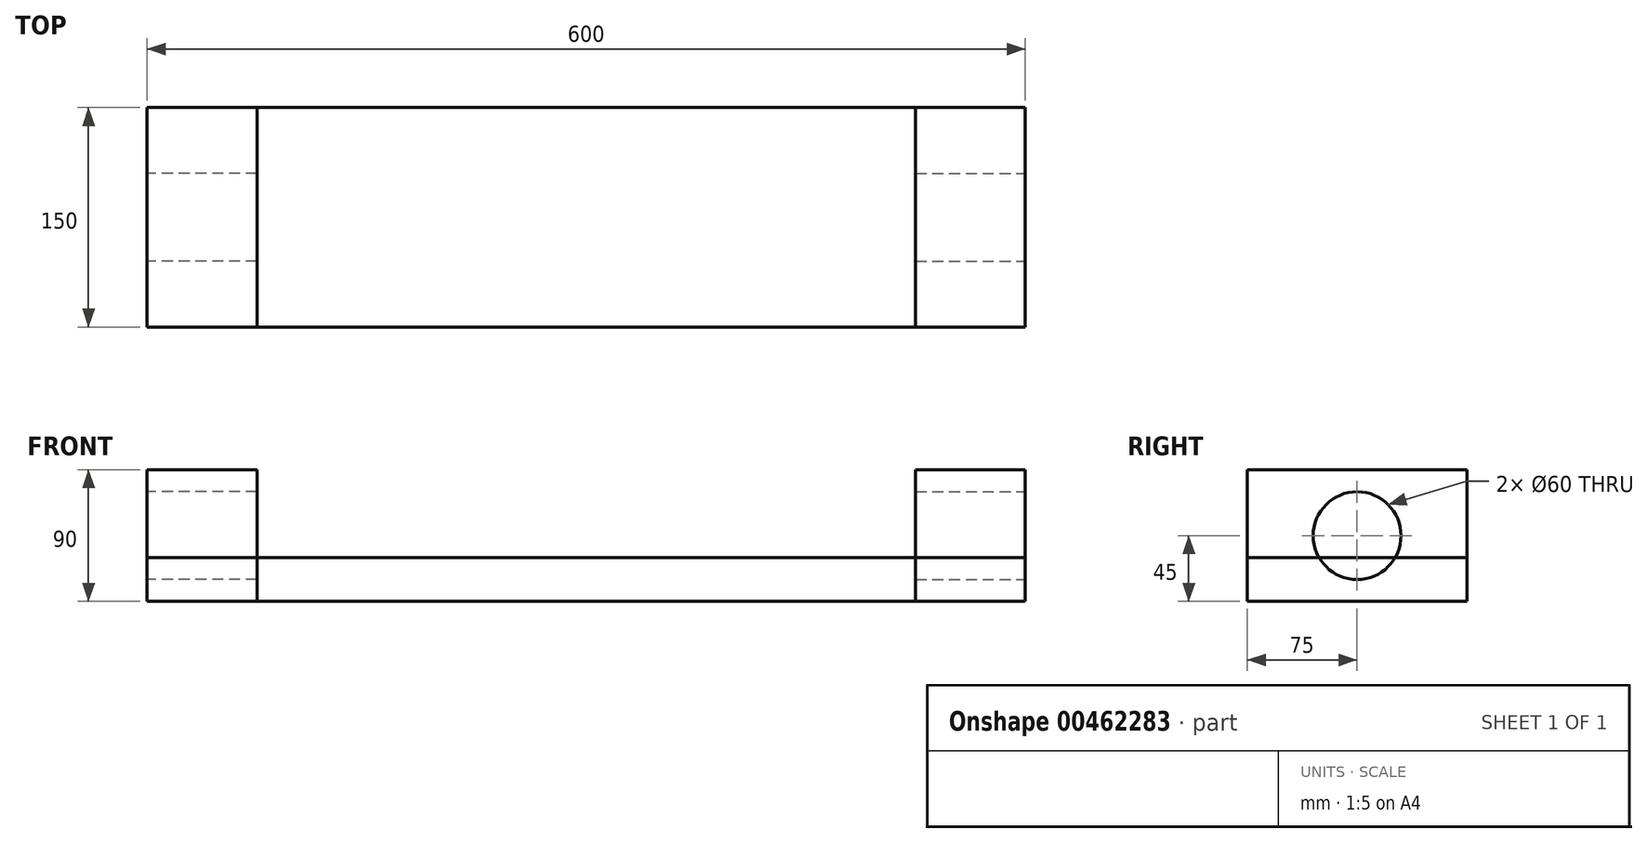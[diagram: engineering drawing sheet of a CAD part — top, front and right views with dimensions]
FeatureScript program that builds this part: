
annotation { "Feature Type Name" : "Feature", "Feature Type Description" : "" }
export const myFeature = defineFeature(function(context is Context, id is Id, definition is map)
    precondition{}
    {
        {
            var Q0;
            Q0=qCreatedBy(makeId("Top.planeOp"),FACE);
            var sketch = newSketch(context, id + "F0", { "sketchPlane" : qUnion([Q0])});
            skLineSegment(sketch, "E0.bottom", {"start": v(300, 75) * mm, "end": v(-300, 75) * mm});
            skLineSegment(sketch, "E0.top", {"start": v(300, -75) * mm, "end": v(-300, -75) * mm});
            skLineSegment(sketch, "E0.left", {"start": v(300, 75) * mm, "end": v(300, -75) * mm});
            skLineSegment(sketch, "E0.right", {"start": v(-300, 75) * mm, "end": v(-300, -75) * mm});
            skPoint(sketch, "E0.middle", {"position": v(0, 0) * mm});
            skLineSegment(sketch, "E1.bottom", {"start": v(300, -75) * mm, "end": v(225, -75) * mm});
            skLineSegment(sketch, "E1.top", {"start": v(300, 75) * mm, "end": v(225, 75) * mm});
            skLineSegment(sketch, "E1.left", {"start": v(300, -75) * mm, "end": v(300, 75) * mm});
            skLineSegment(sketch, "E1.right", {"start": v(225, -75) * mm, "end": v(225, 75) * mm});
            skLineSegment(sketch, "E2.bottom", {"start": v(-300, -75) * mm, "end": v(-225, -75) * mm});
            skLineSegment(sketch, "E2.top", {"start": v(-300, 75) * mm, "end": v(-225, 75) * mm});
            skLineSegment(sketch, "E2.left", {"start": v(-300, -75) * mm, "end": v(-300, 75) * mm});
            skLineSegment(sketch, "E2.right", {"start": v(-225, -75) * mm, "end": v(-225, 75) * mm});
            skSolve(sketch);
        }
        {
            var Q0;
            Q0=qCreatedBy(makeId("Right.planeOp"),FACE);
            var sketch = newSketch(context, id + "F1", { "sketchPlane" : qUnion([Q0])});
            skLineSegment(sketch, "E3.bottom", {"start": v(73.99, 0) * mm, "end": v(-76.01, 0) * mm});
            skLineSegment(sketch, "E3.top", {"start": v(73.99, 90) * mm, "end": v(-76.01, 90) * mm});
            skLineSegment(sketch, "E3.left", {"start": v(73.99, 0) * mm, "end": v(73.99, 90) * mm});
            skLineSegment(sketch, "E3.right", {"start": v(-76.01, 0) * mm, "end": v(-76.01, 90) * mm});
            skSolve(sketch);
        }
        {
            var Q0;
            Q0=makeQuery(id+"F1.imprint","IMPRINT",FACE,{"disambiguationData":[TD([[makeQuery(id+"F1.imprint","IMPRINT",EDGE,{"derivedFrom":sQuery(id+"F1.wireOp",EDGE,"E3.bottom")}),-1.0]])]});
            cPlane(context, id + "F2", {"entities" : qUnion([Q0]), "cplaneType" : CPlaneType.OFFSET, "offset" : 300 * mm, "width" : 150 * mm, "height" : 150 * mm});
        }
        {
            var Q0;
            Q0=qCreatedBy(id+"F2.planeOp",FACE);
            var sketch = newSketch(context, id + "F3", { "sketchPlane" : qUnion([Q0])});
            skLineSegment(sketch, "E4", {"start": v(0, 0) * mm, "end": v(0, 45) * mm});
            skLineSegment(sketch, "E5.bottom", {"start": v(75, 0) * mm, "end": v(-75, 0) * mm});
            skLineSegment(sketch, "E5.top", {"start": v(75, 90) * mm, "end": v(-75, 90) * mm});
            skLineSegment(sketch, "E5.left", {"start": v(75, 0) * mm, "end": v(75, 90) * mm});
            skLineSegment(sketch, "E5.right", {"start": v(-75, 0) * mm, "end": v(-75, 90) * mm});
            skPoint(sketch, "E5.middle", {"position": v(0, 45) * mm});
            skCircle(sketch, "E6", {"center": v(0, 45) * mm, "radius": 30 * mm});
            skSolve(sketch);
        }
        {
            var Q0;
            Q0 = qSketchRegion(id + "F3", true);
            extrude(context, id + "F4", {"entities" : qUnion([Q0]), "oppositeDirection" : true, "depth" : 75 * mm});
        }
        {
            var Q0;
            Q0=makeQuery(id+"F1.imprint","IMPRINT",FACE,{"disambiguationData":[TD([[makeQuery(id+"F1.imprint","IMPRINT",EDGE,{"derivedFrom":sQuery(id+"F1.wireOp",EDGE,"E3.bottom")}),-1.0]])]});
            cPlane(context, id + "F5", {"entities" : qUnion([Q0]), "cplaneType" : CPlaneType.OFFSET, "offset" : 300 * mm, "oppositeDirection" : true, "width" : 150 * mm, "height" : 150 * mm});
        }
        {
            var Q0;
            Q0=qCreatedBy(id+"F5.planeOp",FACE);
            var sketch = newSketch(context, id + "F6", { "sketchPlane" : qUnion([Q0])});
            skLineSegment(sketch, "E7", {"start": v(0, 0) * mm, "end": v(0, 45) * mm});
            skLineSegment(sketch, "E8.bottom", {"start": v(-75, 90) * mm, "end": v(75, 90) * mm});
            skLineSegment(sketch, "E8.top", {"start": v(-75, 0) * mm, "end": v(75, 0) * mm});
            skLineSegment(sketch, "E8.left", {"start": v(-75, 90) * mm, "end": v(-75, 0) * mm});
            skLineSegment(sketch, "E8.right", {"start": v(75, 90) * mm, "end": v(75, 0) * mm});
            skPoint(sketch, "E8.middle", {"position": v(0, 45) * mm});
            skCircle(sketch, "E9", {"center": v(0, 45) * mm, "radius": 30 * mm});
            skSolve(sketch);
        }
        {
            var Q0;
            Q0 = qSketchRegion(id + "F6", true);
            extrude(context, id + "F7", {"entities" : qUnion([Q0]), "depth" : 75 * mm});
        }
        {
            var Q0;
            Q0=makeQuery(id+"F0.imprint","IMPRINT",FACE,{"disambiguationData":[TD([[makeQuery(id+"F0.imprint","IMPRINT",EDGE,{"derivedFrom":sQuery(id+"F0.wireOp",EDGE,"E0.bottom")}),1.0]])]});
            extrude(context, id + "F8", {"entities" : qUnion([Q0]), "depth" : 30 * mm});
        }
    });
